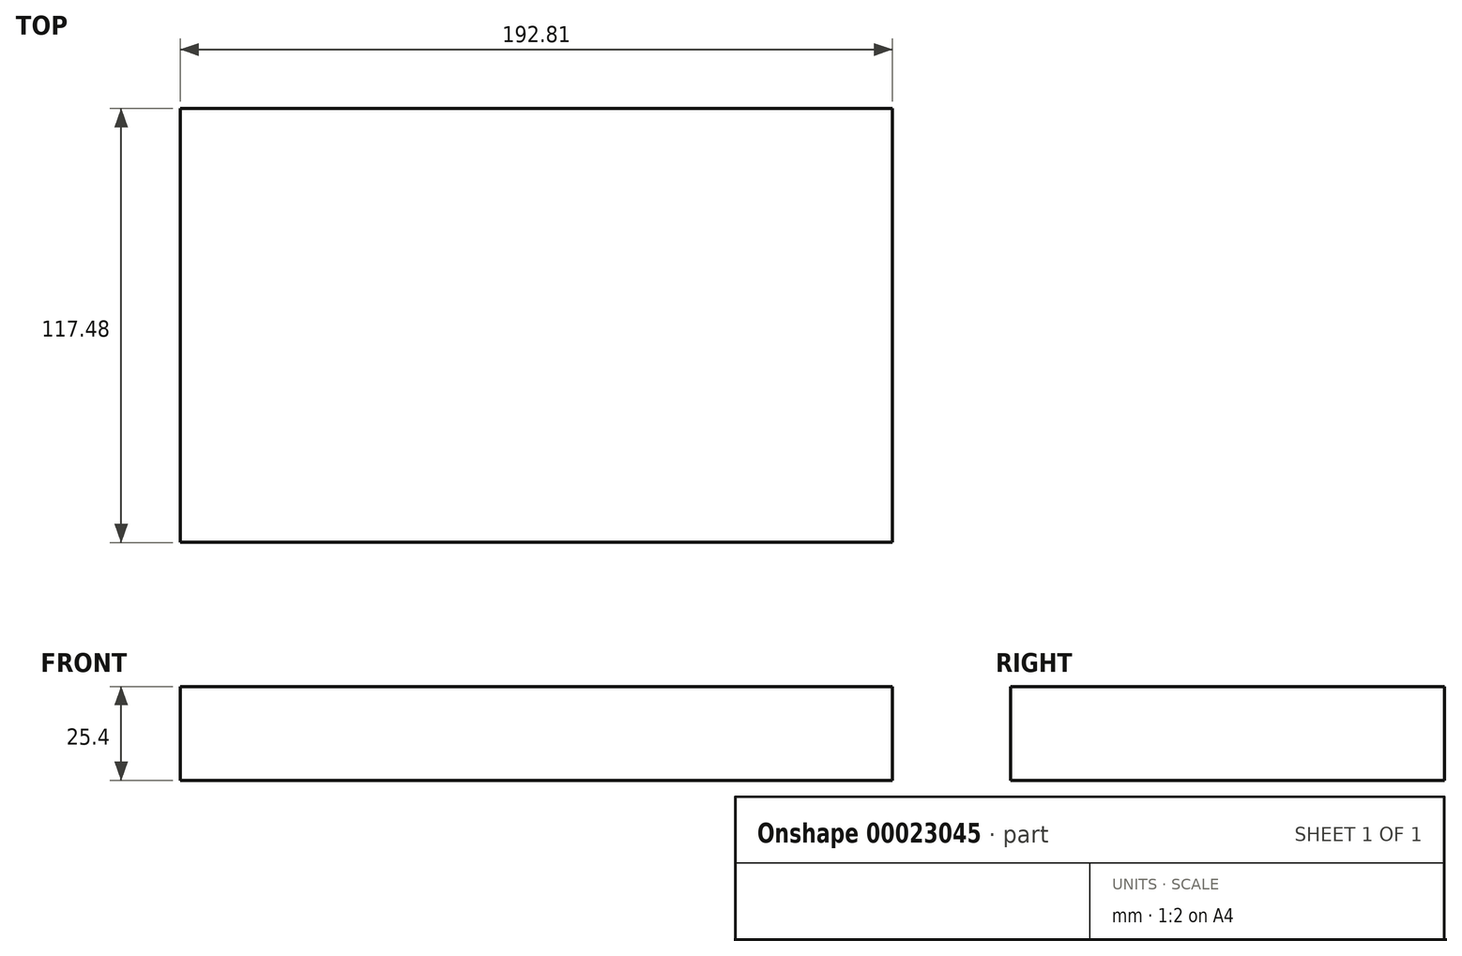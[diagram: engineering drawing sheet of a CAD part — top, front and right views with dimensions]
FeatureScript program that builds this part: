
annotation { "Feature Type Name" : "Feature", "Feature Type Description" : "" }
export const myFeature = defineFeature(function(context is Context, id is Id, definition is map)
    precondition{}
    {
        {
            var Q0;
            Q0=qCreatedBy(makeId("Top.planeOp"),FACE);
            var sketch = newSketch(context, id + "F0", { "sketchPlane" : qUnion([Q0])});
            skLineSegment(sketch, "E0.bottom", {"start": v(-89.93, 56.58) * mm, "end": v(102.88, 56.58) * mm});
            skLineSegment(sketch, "E0.top", {"start": v(-89.93, -60.9) * mm, "end": v(102.88, -60.9) * mm});
            skLineSegment(sketch, "E0.left", {"start": v(-89.93, 56.58) * mm, "end": v(-89.93, -60.9) * mm});
            skLineSegment(sketch, "E0.right", {"start": v(102.88, 56.58) * mm, "end": v(102.88, -60.9) * mm});
            skSolve(sketch);
        }
        {
            var Q0;
            Q0=makeQuery(id+"F0.imprint","IMPRINT",FACE,{"disambiguationData":[TD([[makeQuery(id+"F0.imprint","IMPRINT",EDGE,{"derivedFrom":sQuery(id+"F0.wireOp",EDGE,"E0.bottom")}),-1.0]])]});
            extrude(context, id + "F1", {"entities" : qUnion([Q0]), "depth" : 25.4 * mm});
        }
    });
